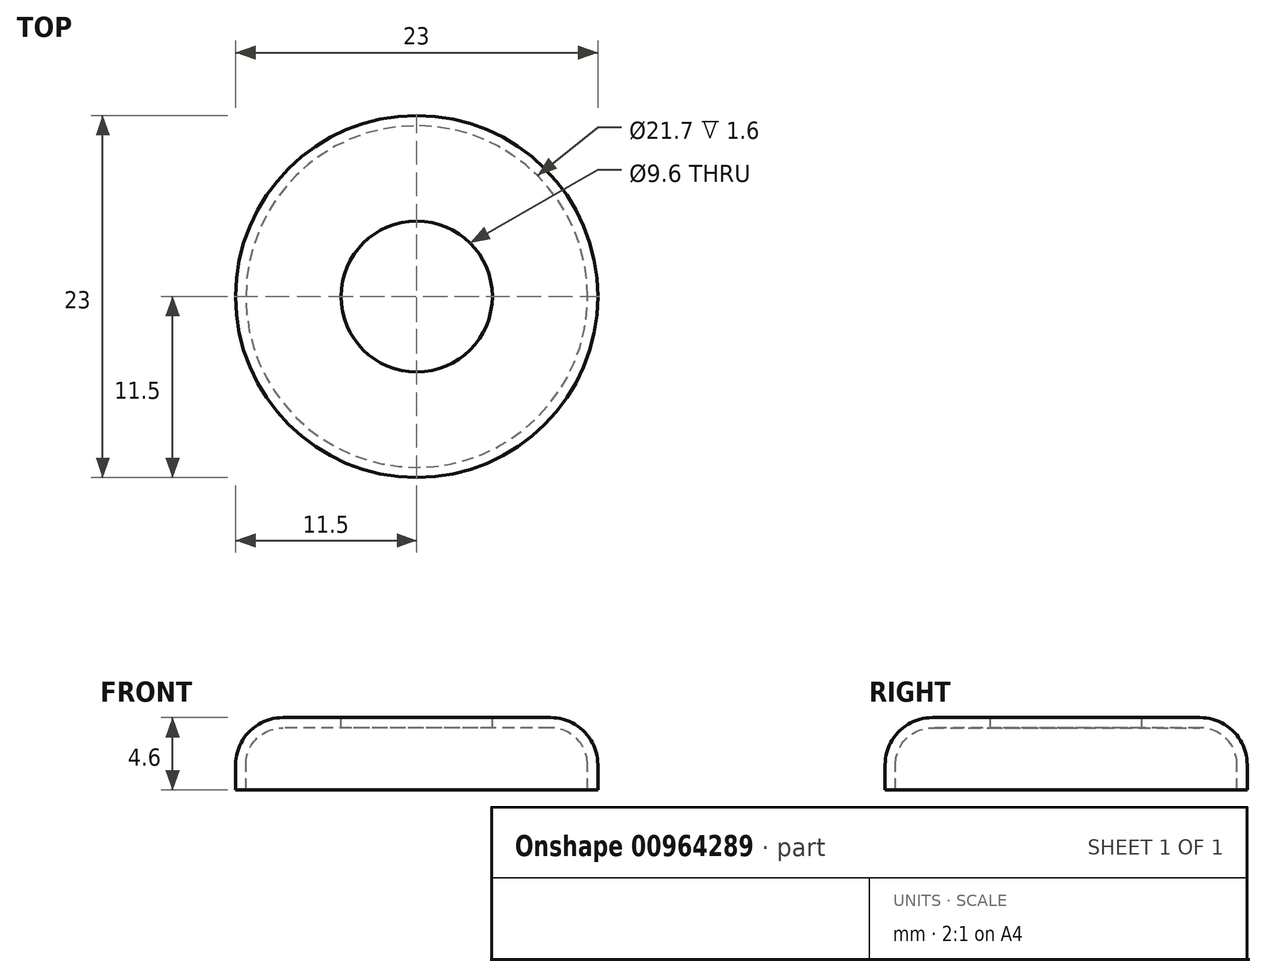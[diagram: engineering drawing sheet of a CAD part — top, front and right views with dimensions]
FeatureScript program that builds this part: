
annotation { "Feature Type Name" : "Feature", "Feature Type Description" : "" }
export const myFeature = defineFeature(function(context is Context, id is Id, definition is map)
    precondition{}
    {
        {
            var Q0;
            Q0=qCreatedBy(makeId("Front.planeOp"),FACE);
            var sketch = newSketch(context, id + "F0", { "sketchPlane" : qUnion([Q0])});
            skLineSegment(sketch, "E0.bottom", {"start": v(0, 0) * mm, "end": v(8.5, 0) * mm});
            skLineSegment(sketch, "E0.top", {"start": v(0, -4.6) * mm, "end": v(11.5, -4.6) * mm});
            skLineSegment(sketch, "E0.left", {"start": v(0, 0) * mm, "end": v(0, -4.6) * mm});
            skLineSegment(sketch, "E0.right", {"start": v(11.5, -3) * mm, "end": v(11.5, -4.6) * mm});
            skPoint(sketch, "E1.visualSharp", {"position": v(11.5, 0) * mm});
            skArc(sketch, "E1.filletArc", {"start": v(11.5, -3) * mm, "mid": v(10.62, -0.88) * mm, "end": v(8.5, 0) * mm});
            skSolve(sketch);
        }
        {
            var Q0;
            Q0 = qSketchRegion(id + "F0", true);
            var Q1;
            Q1=sQuery(id+"F0.wireOp",EDGE,"E0.left");
            revolve(context, id + "F1", {"surfaceOperationType" : NewSurfaceOperationType.NEW, "entities" : qUnion([Q0]), "axis" : qUnion([Q1]), "revolveType" : RevolveType.FULL});
        }
        {
            var Q0;
            Q0=makeQuery(id+"F1.opRevolve","SWEPT_FACE",FACE,{"disambiguationData":[OSD([sQuery(id+"F0.wireOp",EDGE,"E0.top")])]});
            shell(context, id + "F2", {"entities" : qUnion([Q0]), "thickness" : .65 * mm});
        }
        {
            var Q0;
            Q0=makeQuery(id+"F1.opRevolve","SWEPT_FACE",FACE,{"disambiguationData":[OSD([sQuery(id+"F0.wireOp",EDGE,"E0.bottom")])]});
            var sketch = newSketch(context, id + "F3", { "sketchPlane" : qUnion([Q0])});
            skCircle(sketch, "E2", {"center": v(0, 0) * mm, "radius": 4.8 * mm});
            skSolve(sketch);
        }
        {
            var Q0;
            Q0 = qSketchRegion(id + "F3", true);
            extrude(context, id + "F4", {"entities" : qUnion([Q0]), "operationType" : NewBodyOperationType.REMOVE, "endBound" : BoundingType.THROUGH_ALL, "oppositeDirection" : true, "depth" : 25 * mm, "offsetDistance" : 25 * mm});
        }
    });
